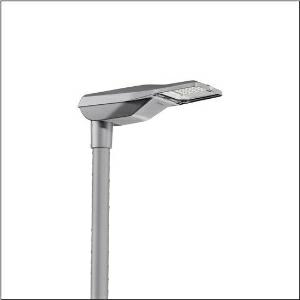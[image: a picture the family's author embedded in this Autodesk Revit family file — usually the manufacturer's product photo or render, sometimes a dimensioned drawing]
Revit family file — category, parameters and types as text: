
# Revit family: streetlight_sl_21_iq_micro___p0_8ab_5xe1r31d08db_6a63
name_source: partatom
category: Lighting Fixtures
units: mm (PartAtom-declared; Revit-internal decimal feet)

## family parameters
Cut with Voids When Loaded = No
Host = Face
Light Source = No
Part Type = Normal
Room Calculation Point = No
Round Connector Dimension = Use Diameter
Shared = No

## types (1)
- --- (1 x LED, 4220 lm, 36.4 W, 3000K)
    Apparent Load = 36 VA
    CIE Flux Codes = 36 71 98 100 100
    Color Rendering = 70
    Color Temperature = 3000K
    Default Elevation = 1800 mm
    Description = Streetlight SL 21 iQ micro, mast luminaire, primary light control with lens, of PMMA, primary optical cover: cover, of toughened safety glass, transparent, light distribution: P0.8aB, light emission: direct distribution, primary light characteristic: asymmetric, installation type: post-top, side-entry, LED, High Power LED, rated luminous flux: 4.220lm, luminous efficacy: 116lm/W, light colour: 730, colour temperature: 3000K, control gear: iQ-Comfort, control: pre-setting: linear dimming characteristic, Auto-Match, Temp-Guard, Lumen-Switch, Night-Set, Smart-Wire, Light-Fading, Desk-Remote (wireless, voltage-free reading and setting of iQ features in the workshop via application-optimized NFC function/RFID function), optimised constant luminous flux control (CLO 2.0), mains connection: 220..240V, AC, 50/60Hz, start of lifetime: 36W, end of service life: 38W, reduction: 16W, luminaire housing, of diecast aluminium, powder-coated, Siteco® metallic grey (DB 702S), corrosivity category C5 mid according to DIN EN ISO 12944, please order mast flange separately, inclination adjustable: 0°, 5°, 10°, 15°, sealing non-destructively replaceable, multi-level sealing system, length: 528mm, width: 235mm, height: 110mm, mast flange for spigot size: 42mm (side-entry): 5XC10008XM4, 60/48mm (side-entry/post-top): 5XC10108XM2, 76/60mm (side-entry/post-top): 5XC10108XM1, protection rating (complete): IP66, insulation class (complete): insulation class II (safety insulation), certification: CE, ENEC, ENEC+, VDE, impact resistance: IK10, permissible operating ambient temperature for outdoor applications: -40..+50°C, standard-compliant lighting for roads and squares, packaging unit: 1 piece

Light Distribution: P0.8aB
    Height = 110 mm
    Lamp = 1 x LED
    Lamp Light Flux = 4220 lm
    Lamp Power = 36.4 W
    Lamp count = 1
    Length = 528 mm
    Luminous efficacy = 116 lm/W
    Manufacturer = Siteco
    ModVariant = No
    Model = 5XE1R31D08DB
    Number of Poles = 1
    OnlyDefault = Yes
    Power Factor = 1
    Product Name = Streetlight SL 21 iQ micro | P0.8aB
    Product group = mast luminaire | pylon top
    ProductGroupID = 6100
    Protection Class = Protection class II
    Protection Degree = IP 66
    RLX_Detail_Level = 1
    RLX_Emergency_Light_Flux = 0 lm
    RLX_Emergency_Type = 0
    RLX_Emergency_Type_DB = No
    RlxData = <blob elided: 98677 chars, md5=19917c92>
    Socket = socket
    Standby Power = 0 W
    System Light Flux = 4220 lm
    System Power = 36 W
    Type Comments = factory setting: luminous flux: 100 % | dim-lin: 254 | 715 mA
    Type Image = l_1006881.jpg
    URL = http://relux.com
    VarID = @adj_074822
    Voltage = 0 V
    Weight = 0.00 kg
    Width = 235 mm

## geometry (parser evidence)
native form markers: Blend x4, Sweep x9
no freeform markers — native parametric forms only
